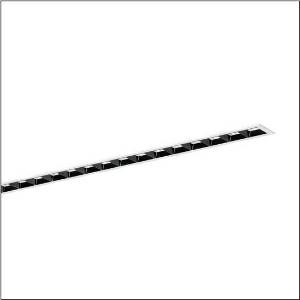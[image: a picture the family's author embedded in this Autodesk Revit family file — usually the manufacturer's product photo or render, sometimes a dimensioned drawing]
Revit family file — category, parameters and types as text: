
# Revit family: silica_r__21_51mx11da44wb_a581
name_source: partatom
category: Lighting Fixtures
units: mm (PartAtom-declared; Revit-internal decimal feet)

## family parameters
Cut with Voids When Loaded = No
Host = Face
Light Source = No
Part Type = Normal
Room Calculation Point = No
Round Connector Dimension = Use Diameter
Shared = No

## types (1)
- --- (1 x LED, 4320 lm, 25.6 W, 4000K)
    Apparent Load = 26 VA
    CIE Flux Codes = 87 99 100 100 100
    Color Rendering = 80
    Color Temperature = 4000K
    Default Elevation = 1800 mm
    Description = Silica® 21, office luminaire, primary light control with darklight reflector, of PMMA, black, CAT 2 (L<= 3000cd/m²), light emission: direct distribution, primary light characteristic: symmetric, installation type: recessed, LED, rated luminous flux: 4.320lm, luminous efficacy: 169lm/W, light colour: 840, colour temperature: 4000K, control gear: DALI 2, with terminal, 3+2-pole, max. 2.5mm², mains connection: 220..240V, AC, 50/60Hz, rated input power: 25.6W, luminaire housing, of aluminium, traffic white (RAL 9016), length: 1.228mm, width: 79mm, height: 53mm, protection rating (complete): IP20, insulation class (complete): insulation class I (protective earthing), certification: CE, ENEC, VDE, permissible operating ambient temperature: 0..+35°C, standard: EN 50419, packaging unit: 1 piece
    Height = 0 mm  [stored 0 ft]
    Lamp = 1 x LED
    Lamp Light Flux = 4320 lm
    Lamp Power = 25.6 W
    Lamp count = 1
    Length = 1227 mm
    Luminous efficacy = 169 lm/W
    Manufacturer = Siteco
    ModVariant = No
    Model = 51MX11DA44WB
    Mounting Place = Ceiling
    Mounting Type = Recessed
    Number of Poles = 1
    OnlyDefault = Yes
    Power Factor = 1
    Product Name = Silica® 21
    Product group = office luminaire | ceiling recessed
    ProductGroupID = 401
    Protection Class = Protection class I
    Protection Degree = IP 20
    RLX_Detail_Level = 1
    RLX_Emergency_Light_Flux = 0 lm
    RLX_Emergency_Type = 0
    RLX_Emergency_Type_DB = No
    RlxData = <blob elided: 39865 chars, md5=87ca283c>
    Socket = socket
    Standby Power = 0 W
    System Light Flux = 4320 lm
    System Power = 26 W
    Type Comments = factory setting: luminous flux: 100 % | dim-lin: 254 | 367 mA
    Type Image = l_1335880.jpg
    URL = http://relux.com
    VarID = @adj_008121
    Voltage = 0 V
    Weight = 0.00 kg
    Width = 79 mm

note: [stored X ft] marks values corroborated as IEEE doubles in the binary element streams (Revit-internal decimal feet)

## geometry (parser evidence)
native form markers: Blend x4, Sweep x11
no freeform markers — native parametric forms only
